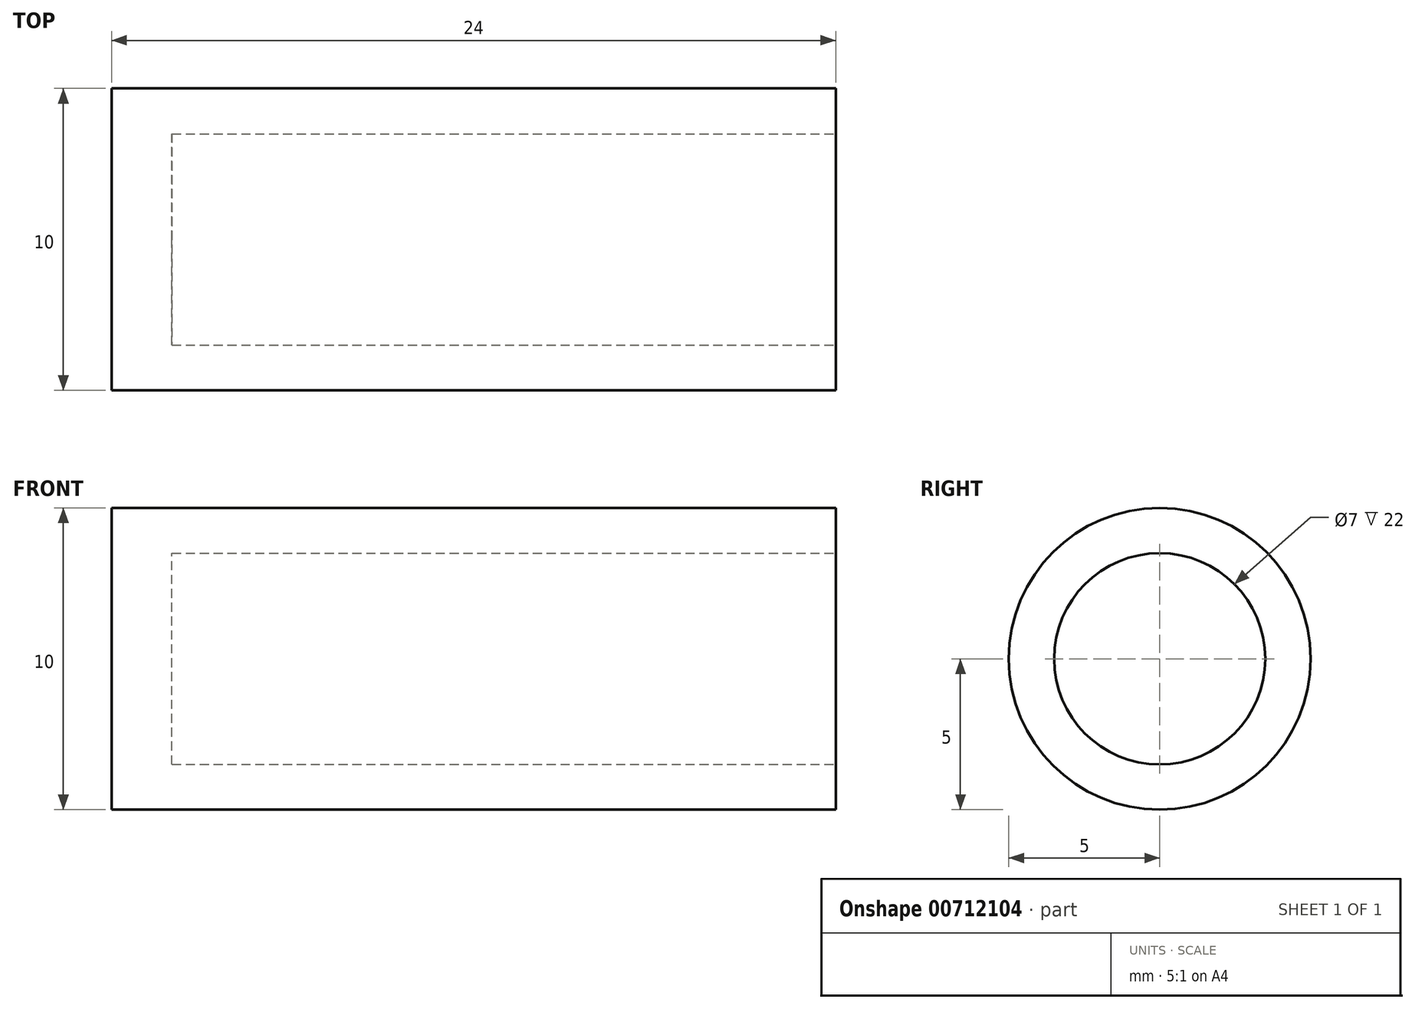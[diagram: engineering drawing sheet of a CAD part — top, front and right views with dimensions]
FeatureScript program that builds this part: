
annotation { "Feature Type Name" : "Feature", "Feature Type Description" : "" }
export const myFeature = defineFeature(function(context is Context, id is Id, definition is map)
    precondition{}
    {
        {
            var Q0;
            Q0=qCreatedBy(makeId("Right.planeOp"),FACE);
            var sketch = newSketch(context, id + "F0", { "sketchPlane" : qUnion([Q0])});
            skCircle(sketch, "E0", {"center": v(0, 0) * mm, "radius": 5 * mm});
            skCircle(sketch, "E1", {"center": v(0, 0) * mm, "radius": 3.5 * mm});
            skSolve(sketch);
        }
        {
            var Q0;
            Q0=qSketchRegion(id+"F0",true);
            var Q1;
            Q1=makeQuery(id+"F0.imprint","IMPRINT",FACE,{"disambiguationData":[TD([[makeQuery(id+"F0.imprint","IMPRINT",EDGE,{"derivedFrom":sQuery(id+"F0.wireOp",EDGE,"E1")}),1.0]])]});
            extrude(context, id + "F1", {"entities" : qUnion([Q0, Q1]), "oppositeDirection" : true, "depth" : 24 * mm, "offsetDistance" : 25 * mm});
        }
        {
            var Q0;
            Q0=makeQuery(id+"F0.imprint","IMPRINT",FACE,{"disambiguationData":[TD([[makeQuery(id+"F0.imprint","IMPRINT",EDGE,{"derivedFrom":sQuery(id+"F0.wireOp",EDGE,"E1")}),1.0]])]});
            extrude(context, id + "F2", {"entities" : qUnion([Q0]), "operationType" : NewBodyOperationType.REMOVE, "oppositeDirection" : true, "depth" : 22 * mm, "offsetDistance" : 25 * mm});
        }
    });
